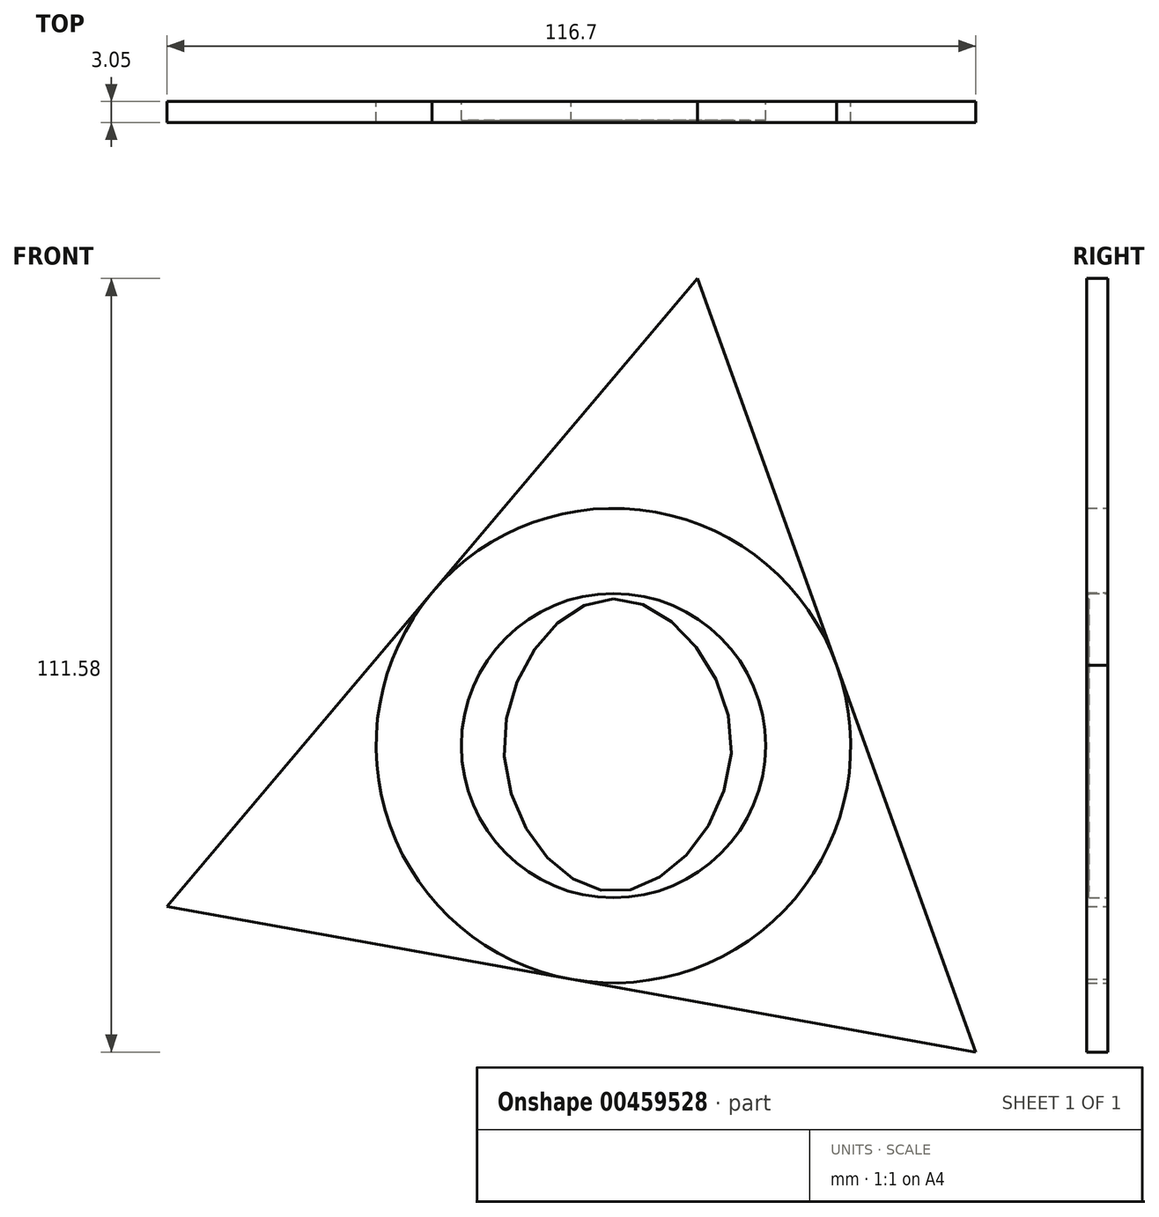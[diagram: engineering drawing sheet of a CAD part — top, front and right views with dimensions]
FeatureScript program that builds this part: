
annotation { "Feature Type Name" : "Feature", "Feature Type Description" : "" }
export const myFeature = defineFeature(function(context is Context, id is Id, definition is map)
    precondition{}
    {
        {
            var Q0;
            Q0=qCreatedBy(makeId("Front.planeOp"),FACE);
            var sketch = newSketch(context, id + "F0", { "sketchPlane" : qUnion([Q0])});
            skCircle(sketch, "E0.cCircle", {"center": v(0, 0) * mm, "radius": 34.23 * mm, "construction": true});
            skLineSegment(sketch, "E0.0", {"start": v(-64.42, -23.18) * mm, "end": v(12.14, 67.38) * mm});
            skLineSegment(sketch, "E0.1", {"start": v(12.14, 67.38) * mm, "end": v(52.28, -44.2) * mm});
            skLineSegment(sketch, "E0.2", {"start": v(52.28, -44.2) * mm, "end": v(-64.42, -23.18) * mm});
            skPoint(sketch, "E0.0.midPoint", {"position": v(-26.14, 22.1) * mm});
            skCircle(sketch, "E1", {"center": v(0, 0) * mm, "radius": 34.23 * mm});
            skSolve(sketch);
        }
        {
            var Q0;
            {var subQ0=sQuery(id+"F0.wireOp",EDGE,"E0.2");var subQ1=sQuery(id+"F0.wireOp",EDGE,"E0.0");var subQ2=makeQuery(id+"F0.imprint","INTERSECT",VERTEX,{"derivedFrom":[subQ1,subQ0]});Q0=makeQuery(id+"F0.imprint","IMPRINT",FACE,{"disambiguationData":[TD([[makeQuery(id+"F0.imprint","IMPRINT",EDGE,{"disambiguationData":[TD([[subQ2,-1.0]])],"derivedFrom":subQ1}),-1.0]])]});}
            var Q1;
            {var subQ0=sQuery(id+"F0.wireOp",EDGE,"E0.1");var subQ1=sQuery(id+"F0.wireOp",EDGE,"E0.0");var subQ2=makeQuery(id+"F0.imprint","INTERSECT",VERTEX,{"derivedFrom":[subQ1,subQ0]});Q1=makeQuery(id+"F0.imprint","IMPRINT",FACE,{"disambiguationData":[TD([[makeQuery(id+"F0.imprint","IMPRINT",EDGE,{"disambiguationData":[TD([[subQ2,1.0]])],"derivedFrom":subQ1}),-1.0]])]});}
            var Q2;
            {var subQ0=sQuery(id+"F0.wireOp",EDGE,"E0.2");var subQ1=sQuery(id+"F0.wireOp",EDGE,"E0.1");var subQ2=makeQuery(id+"F0.imprint","INTERSECT",VERTEX,{"derivedFrom":[subQ1,subQ0]});Q2=makeQuery(id+"F0.imprint","IMPRINT",FACE,{"disambiguationData":[TD([[makeQuery(id+"F0.imprint","IMPRINT",EDGE,{"disambiguationData":[TD([[subQ2,1.0]])],"derivedFrom":subQ1}),-1.0]])]});}
            extrude(context, id + "F1", {"entities" : qUnion([Q0, Q1, Q2]), "depth" : 3.05 * mm});
        }
        {
            var Q0;
            Q0=qCreatedBy(makeId("Front.planeOp"),FACE);
            var sketch = newSketch(context, id + "F2", { "sketchPlane" : qUnion([Q0])});
            skFitSpline(sketch, "E2", {"points": [v(0, 21.2) * mm, v(-15.8, 0) * mm, v(0, -21.06) * mm, v(17.02, 0) * mm, v(0, 21.2) * mm]});
            skSolve(sketch);
        }
        {
            var Q0;
            Q0 = qSketchRegion(id + "F2", true);
            extrude(context, id + "F3", {"entities" : qUnion([Q0]), "depth" : 3.05 * mm});
        }
        {
            var Q0;
            Q0=qCreatedBy(makeId("Front.planeOp"),FACE);
            var sketch = newSketch(context, id + "F4", { "sketchPlane" : qUnion([Q0])});
            skFitSpline(sketch, "E3", {"points": [v(0, 11.76) * mm, v(7.7, 0) * mm, v(0, -10.72) * mm, v(-8.93, 0) * mm, v(0, 11.76) * mm]});
            skCircle(sketch, "E4", {"center": v(0, 0) * mm, "radius": 21.94 * mm});
            skSolve(sketch);
        }
        {
            var Q0;
            Q0 = qSketchRegion(id + "F4", true);
            extrude(context, id + "F5", {"entities" : qUnion([Q0]), "operationType" : NewBodyOperationType.ADD, "depth" : 2.74 * mm});
        }
    });
